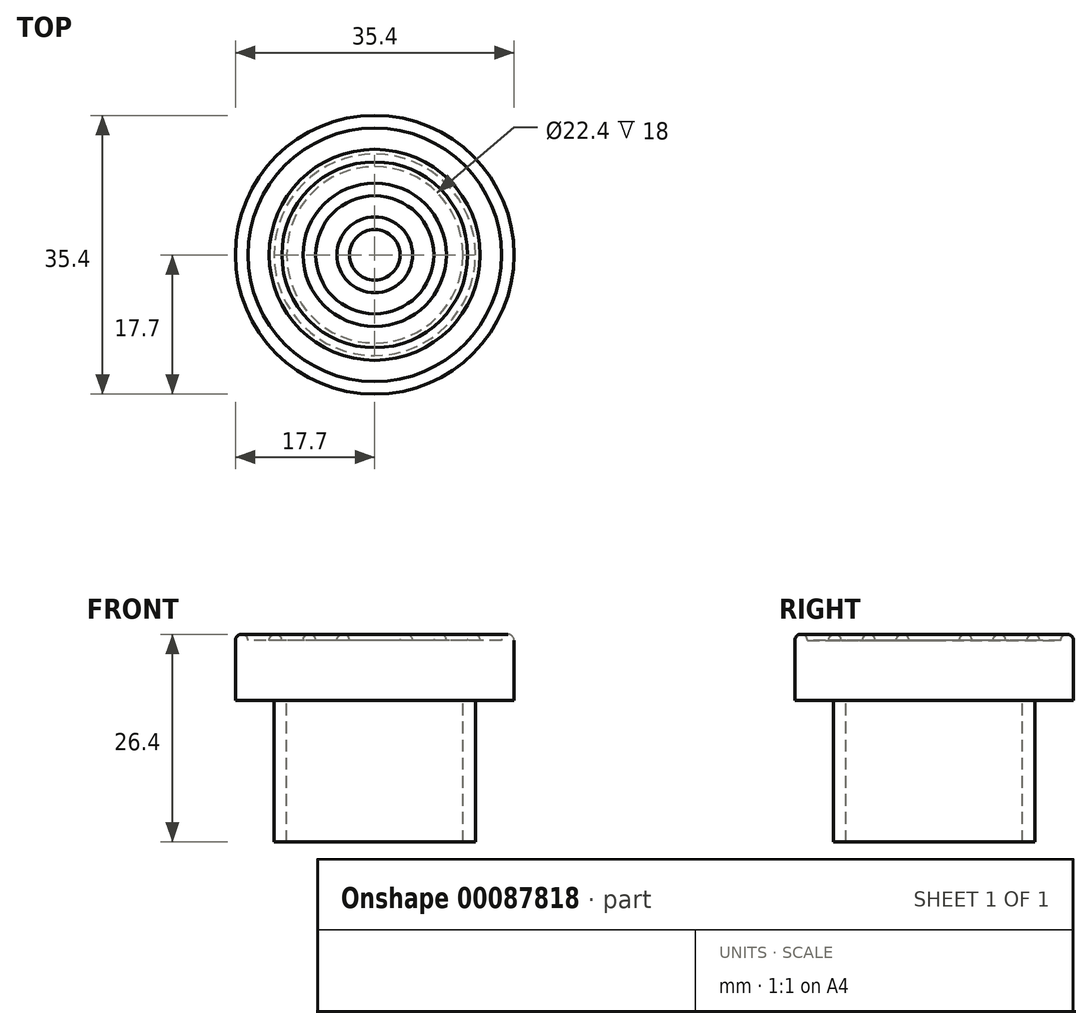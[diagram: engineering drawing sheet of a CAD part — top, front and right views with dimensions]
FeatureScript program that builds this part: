
annotation { "Feature Type Name" : "Feature", "Feature Type Description" : "" }
export const myFeature = defineFeature(function(context is Context, id is Id, definition is map)
    precondition{}
    {
        {
            assignVariable(context, id + "F0", {"name" : "epaisseur", "anyValue" : 7.6});
        }
        {
            var Q0;
            Q0=qCreatedBy(makeId("Top.planeOp"),FACE);
            var sketch = newSketch(context, id + "F1", { "sketchPlane" : qUnion([Q0])});
            skCircle(sketch, "E0", {"center": v(0, 0) * mm, "radius": 17.7 * mm});
            skSolve(sketch);
        }
        {
            var Q0;
            Q0 = qSketchRegion(id + "F1", true);
            extrude(context, id + "F2", {"entities" : qUnion([Q0]), "depth" : (getVariable(context, 'epaisseur')) * mm});
        }
        {
            var Q0;
            Q0=qCreatedBy(makeId("Front.planeOp"),FACE);
            var sketch = newSketch(context, id + "F3", { "sketchPlane" : qUnion([Q0])});
            skLineSegment(sketch, "E1", {"start": v(0, 6.93) * mm, "end": v(0, -6.92) * mm, "construction": true});
            skLineSegment(sketch, "E2", {"start": v(0, 7.6) * mm, "end": v(17.7, 7.6) * mm, "construction": true});
            skArc(sketch, "E3", {"start": v(4.8, 7.6) * mm, "mid": v(4, 8.4) * mm, "end": v(3.2, 7.6) * mm});
            skLineSegment(sketch, "E4.direction1", {"start": v(3.2, 7.6) * mm, "end": v(7.7, 7.6) * mm, "construction": true});
            skLineSegment(sketch, "E5", {"start": v(3.2, 7.6) * mm, "end": v(4.8, 7.6) * mm});
            skLineSegment(sketch, "E6.1.0.0", {"start": v(7.5, 7.6) * mm, "end": v(9.1, 7.6) * mm});
            skArc(sketch, "E6.1.0.1", {"start": v(9.1, 7.6) * mm, "mid": v(8.3, 8.4) * mm, "end": v(7.5, 7.6) * mm});
            skLineSegment(sketch, "E6.2.0.0", {"start": v(11.8, 7.6) * mm, "end": v(13.4, 7.6) * mm});
            skArc(sketch, "E6.2.0.1", {"start": v(13.4, 7.6) * mm, "mid": v(12.6, 8.4) * mm, "end": v(11.8, 7.6) * mm});
            skLineSegment(sketch, "E6.3.0.0", {"start": v(16.1, 7.6) * mm, "end": v(17.7, 7.6) * mm});
            skArc(sketch, "E6.3.0.1", {"start": v(17.7, 7.6) * mm, "mid": v(16.9, 8.4) * mm, "end": v(16.1, 7.6) * mm});
            skLineSegment(sketch, "E6.direction1", {"start": v(3.2, 7.6) * mm, "end": v(7.5, 7.6) * mm, "construction": true});
            skSolve(sketch);
        }
        {
            var Q0;
            Q0 = qSketchRegion(id + "F3", true);
            var Q1;
            Q1=sQuery(id+"F3.wireOp",EDGE,"E1");
            revolve(context, id + "F4", {"operationType" : NewBodyOperationType.ADD, "entities" : qUnion([Q0]), "axis" : qUnion([Q1]), "revolveType" : RevolveType.FULL});
        }
        {
            var Q0;
            Q0=makeQuery(id+"F2.opExtrude","CAP_FACE",FACE,{"disambiguationData":[OSD([sQuery(id+"F1.wireOp",EDGE,"E0")])],"isStart":true});
            var sketch = newSketch(context, id + "F5", { "sketchPlane" : qUnion([Q0])});
            skCircle(sketch, "E7", {"center": v(0, 0) * mm, "radius": 12.8 * mm});
            skCircle(sketch, "E8", {"center": v(0, 0) * mm, "radius": 11.2 * mm});
            skSolve(sketch);
        }
        {
            var Q0;
            Q0 = qSketchRegion(id + "F5", true);
            extrude(context, id + "F6", {"entities" : qUnion([Q0]), "operationType" : NewBodyOperationType.ADD, "depth" : 18 * mm});
        }
    });
